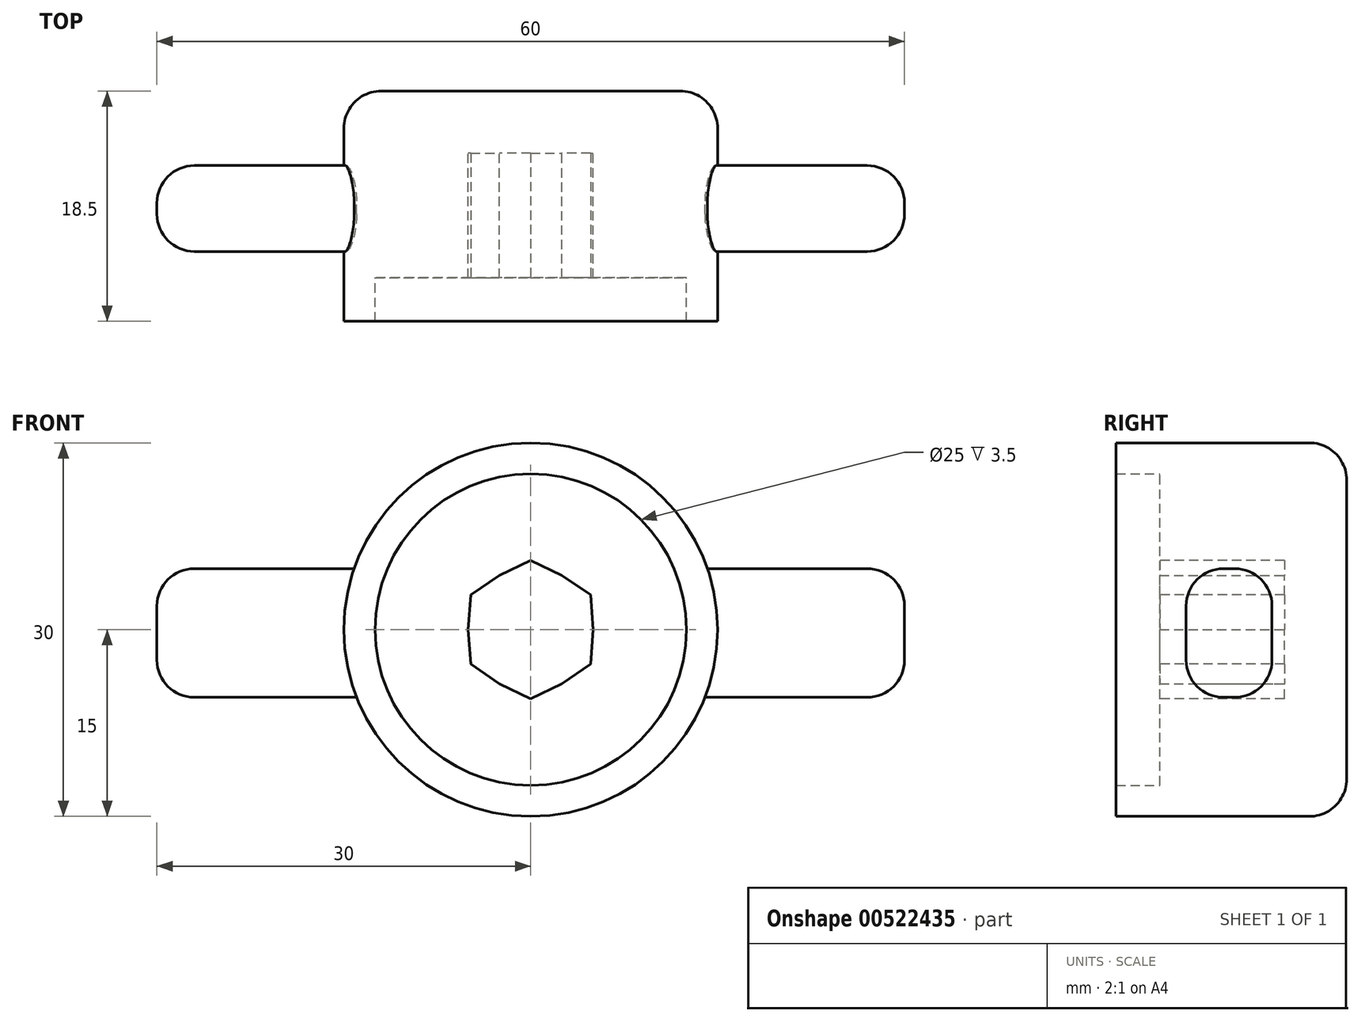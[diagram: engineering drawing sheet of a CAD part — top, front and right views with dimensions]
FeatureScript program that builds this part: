
annotation { "Feature Type Name" : "Feature", "Feature Type Description" : "" }
export const myFeature = defineFeature(function(context is Context, id is Id, definition is map)
    precondition{}
    {
        {
            var Q0;
            Q0=qCreatedBy(makeId("Front.planeOp"),FACE);
            var sketch = newSketch(context, id + "F0", { "sketchPlane" : qUnion([Q0])});
            skCircle(sketch, "E0", {"center": v(0, 0) * mm, "radius": 15 * mm});
            skSolve(sketch);
        }
        {
            var Q0;
            Q0=makeQuery(id+"F0.imprint","IMPRINT",FACE,{"disambiguationData":[TD([[makeQuery(id+"F0.imprint","IMPRINT",EDGE,{"derivedFrom":sQuery(id+"F0.wireOp",EDGE,"E0")}),1.0]])]});
            extrude(context, id + "F1", {"entities" : qUnion([Q0]), "depth" : 18.5 * mm, "offsetDistance" : 25 * mm});
        }
        {
            var Q0;
            Q0=makeQuery(id+"F1.opExtrude","CAP_FACE",FACE,{"disambiguationData":[OSD([sQuery(id+"F0.wireOp",EDGE,"E0")])],"isStart":false});
            shell(context, id + "F2", {"entities" : qUnion([Q0]), "thickness" : 2.5 * mm});
        }
        {
            var Q0;
            {var subQ0=sQuery(id+"F0.wireOp",EDGE,"E0");Q0=makeQuery(id+"F2.opShell","OFFSET_FACE",FACE,{"disambiguationData":[OSD([subQ0]),TDD([makeQuery(id+"F1.opExtrude","CAP_FACE",FACE,{"disambiguationData":[OSD([subQ0])],"isStart":true})])]});}
            var sketch = newSketch(context, id + "F3", { "sketchPlane" : qUnion([Q0])});
            skCircle(sketch, "E1", {"center": v(0, 0) * mm, "radius": 12.5 * mm});
            skSolve(sketch);
        }
        {
            var Q0;
            Q0=makeQuery(id+"F3.imprint","IMPRINT",FACE,{"disambiguationData":[TD([[makeQuery(id+"F3.imprint","IMPRINT",EDGE,{"derivedFrom":sQuery(id+"F3.wireOp",EDGE,"E1")}),1.0]])]});
            extrude(context, id + "F4", {"entities" : qUnion([Q0]), "operationType" : NewBodyOperationType.ADD, "depth" : 12.5 * mm, "offsetDistance" : 25 * mm});
        }
        {
            var Q0;
            Q0=makeQuery(id+"F4.opExtrude","CAP_FACE",FACE,{"disambiguationData":[OSD([sQuery(id+"F3.wireOp",EDGE,"E1")])],"isStart":false});
            var sketch = newSketch(context, id + "F5", { "sketchPlane" : qUnion([Q0])});
            skCircle(sketch, "E2.cCircle", {"center": v(0, 0) * mm, "radius": 5 * mm, "construction": true});
            skLineSegment(sketch, "E2.0", {"start": v(-0.41, 5.76) * mm, "end": v(4.78, 3.24) * mm});
            skLineSegment(sketch, "E2.1", {"start": v(4.78, 3.24) * mm, "end": v(5.2, -2.52) * mm});
            skLineSegment(sketch, "E2.2", {"start": v(5.2, -2.52) * mm, "end": v(0.41, -5.76) * mm});
            skLineSegment(sketch, "E2.3", {"start": v(0.41, -5.76) * mm, "end": v(-4.78, -3.24) * mm});
            skLineSegment(sketch, "E2.4", {"start": v(-4.78, -3.24) * mm, "end": v(-5.2, 2.52) * mm});
            skLineSegment(sketch, "E2.5", {"start": v(-5.2, 2.52) * mm, "end": v(-0.41, 5.76) * mm});
            skPoint(sketch, "E2.0.midPoint", {"position": v(2.18, 4.5) * mm});
            skSolve(sketch);
        }
        {
            var Q0;
            Q0=makeQuery(id+"F5.imprint","IMPRINT",FACE,{"disambiguationData":[TD([[makeQuery(id+"F5.imprint","IMPRINT",EDGE,{"derivedFrom":sQuery(id+"F5.wireOp",EDGE,"E2.0")}),-1.0]])]});
            extrude(context, id + "F6", {"entities" : qUnion([Q0]), "operationType" : NewBodyOperationType.REMOVE, "oppositeDirection" : true, "depth" : 10 * mm, "offsetDistance" : 25 * mm});
        }
        {
            var Q0;
            Q0=qCreatedBy(makeId("Right.planeOp"),FACE);
            cPlane(context, id + "F7", {"entities" : qUnion([Q0]), "cplaneType" : CPlaneType.OFFSET, "offset" : 15 * mm, "width" : 150 * mm, "height" : 150 * mm});
        }
        {
            var Q0;
            Q0=qCreatedBy(id+"F7.planeOp",FACE);
            var sketch = newSketch(context, id + "F8", { "sketchPlane" : qUnion([Q0])});
            skLineSegment(sketch, "E3.bottom", {"start": v(-12.88, 4.9) * mm, "end": v(-5.99, 4.9) * mm});
            skLineSegment(sketch, "E3.top", {"start": v(-12.88, -5.44) * mm, "end": v(-5.99, -5.44) * mm});
            skLineSegment(sketch, "E3.left", {"start": v(-12.88, 4.9) * mm, "end": v(-12.88, -5.44) * mm});
            skLineSegment(sketch, "E3.right", {"start": v(-5.99, 4.9) * mm, "end": v(-5.99, -5.44) * mm});
            skSolve(sketch);
        }
        {
            var Q0;
            Q0=makeQuery(id+"F8.imprint","IMPRINT",FACE,{"disambiguationData":[TD([[makeQuery(id+"F8.imprint","IMPRINT",EDGE,{"derivedFrom":sQuery(id+"F8.wireOp",EDGE,"E3.bottom")}),-1.0]])]});
            extrude(context, id + "F9", {"entities" : qUnion([Q0]), "operationType" : NewBodyOperationType.REMOVE, "oppositeDirection" : true, "depth" : 3 * mm, "offsetDistance" : 25 * mm});
        }
        {
            var Q0;
            Q0=makeQuery(id+"F9.boolean.opBoolean","COPY",FACE,{"derivedFrom":makeQuery(id+"F9.opExtrude","CAP_FACE",FACE,{"disambiguationData":[OSD([sQuery(id+"F8.wireOp",EDGE,"E3.bottom"),sQuery(id+"F8.wireOp",EDGE,"E3.top"),sQuery(id+"F8.wireOp",EDGE,"E3.left"),sQuery(id+"F8.wireOp",EDGE,"E3.right")])],"isStart":false})});
            var sketch = newSketch(context, id + "F10", { "sketchPlane" : qUnion([Q0])});
            skLineSegment(sketch, "E4.bottom", {"start": v(-12.88, -5.44) * mm, "end": v(-5.99, -5.44) * mm});
            skLineSegment(sketch, "E4.top", {"start": v(-12.88, 4.9) * mm, "end": v(-5.99, 4.9) * mm});
            skLineSegment(sketch, "E4.left", {"start": v(-12.88, -5.44) * mm, "end": v(-12.88, 4.9) * mm});
            skLineSegment(sketch, "E4.right", {"start": v(-5.99, -5.44) * mm, "end": v(-5.99, 4.9) * mm});
            skSolve(sketch);
        }
        {
            var Q0;
            Q0=makeQuery(id+"F10.imprint","IMPRINT",FACE,{"disambiguationData":[TD([[makeQuery(id+"F10.imprint","IMPRINT",EDGE,{"derivedFrom":sQuery(id+"F10.wireOp",EDGE,"E4.bottom")}),1.0]])]});
            extrude(context, id + "F11", {"entities" : qUnion([Q0]), "operationType" : NewBodyOperationType.ADD, "depth" : 18 * mm, "offsetDistance" : 25 * mm});
        }
        {
            var Q0;
            Q0=makeQuery(id+"F11.opExtrude","CAP_EDGE",EDGE,{"disambiguationData":[OSD([sQuery(id+"F10.wireOp",EDGE,"E4.top")])],"isStart":false});
            var Q1;
            Q1=makeQuery(id+"F11.opExtrude","CAP_EDGE",EDGE,{"disambiguationData":[OSD([sQuery(id+"F10.wireOp",EDGE,"E4.bottom")])],"isStart":false});
            var Q2;
            Q2=makeQuery(id+"F11.opExtrude","CAP_EDGE",EDGE,{"disambiguationData":[OSD([sQuery(id+"F10.wireOp",EDGE,"E4.right")])],"isStart":false});
            var Q3;
            Q3=makeQuery(id+"F11.opExtrude","CAP_EDGE",EDGE,{"disambiguationData":[OSD([sQuery(id+"F10.wireOp",EDGE,"E4.left")])],"isStart":false});
            var Q4;
            Q4=makeQuery(id+"F11.opExtrude","SWEPT_EDGE",EDGE,{"disambiguationData":[OSD([sQuery(id+"F10.wireOp",EDGE,"E4.top"),sQuery(id+"F10.wireOp",EDGE,"E4.left")])]});
            var Q5;
            Q5=makeQuery(id+"F11.opExtrude","SWEPT_EDGE",EDGE,{"disambiguationData":[OSD([sQuery(id+"F10.wireOp",EDGE,"E4.bottom"),sQuery(id+"F10.wireOp",EDGE,"E4.left")])]});
            var Q6;
            Q6=makeQuery(id+"F11.opExtrude","SWEPT_EDGE",EDGE,{"disambiguationData":[OSD([sQuery(id+"F10.wireOp",EDGE,"E4.top"),sQuery(id+"F10.wireOp",EDGE,"E4.right")])]});
            var Q7;
            Q7=makeQuery(id+"F11.opExtrude","SWEPT_EDGE",EDGE,{"disambiguationData":[OSD([sQuery(id+"F10.wireOp",EDGE,"E4.bottom"),sQuery(id+"F10.wireOp",EDGE,"E4.right")])]});
            var Q8;
            Q8=makeQuery(id+"F1.opExtrude","CAP_EDGE",EDGE,{"disambiguationData":[OSD([sQuery(id+"F0.wireOp",EDGE,"E0")])],"isStart":true});
            fillet(context, id + "F12", {"entities" : qUnion([Q0, Q1, Q2, Q3, Q4, Q5, Q6, Q7, Q8]), "radius" : 3 * mm, "tangentPropagation" : true, "allowEdgeOverflow" : false});
        }
        {
            var Q0;
            Q0=makeQuery(id+"F1.opExtrude","SWEPT_BODY",BODY,{"disambiguationData":[OSD([sQuery(id+"F0.wireOp",EDGE,"E0")])]});
            var Q1;
            Q1=qCreatedBy(makeId("Right.planeOp"),FACE);
            mirror(context, id + "F13", {"operationType" : NewBodyOperationType.ADD, "entities" : qUnion([Q0]), "mirrorPlane" : qUnion([Q1])});
        }
    });
